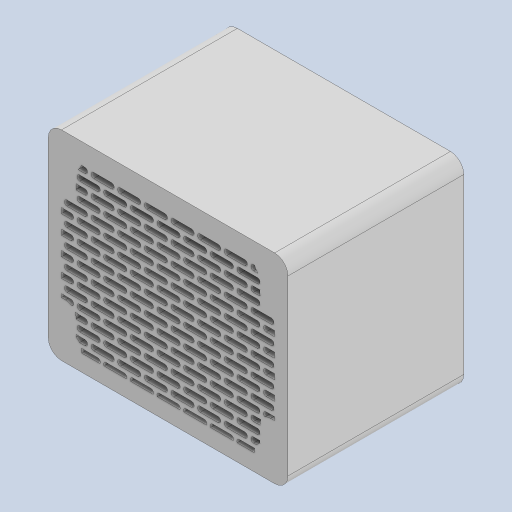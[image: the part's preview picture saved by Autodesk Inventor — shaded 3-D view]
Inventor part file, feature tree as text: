
AUTODESK INVENTOR PART (.ipt)
format: ipt  version: 2023 (Build 270158000, 158)  size: 2,324,480 bytes
history: native  units: mm
features: extrude x11, sketch x11, other x1
ambient origin geometry x8: Origin, YZ Plane, XZ Plane, XY Plane, X Axis, Y Axis, Z Axis, Center Point
bodies: Body1 (feature_tree)
feature tree (23):
  other  "Sólido1"
  extrude  "Extrusão1"  Depth=10.0mm
  extrude  "Extrusão2"  Depth=3.0mm
  extrude  "Extrusão3"  Depth=10.0mm
  extrude  "Extrusão4"  Depth=10.0mm
  extrude  "Extrusão5"  Depth=10.0mm
  extrude  "Extrusão6"  Depth=180.0mm
  extrude  "Extrusão7"  Depth=10.0mm
  extrude  "Extrusão8"  Depth=4.0mm TaperAngle=0.0deg
  extrude  "Extrusão9"  Depth=160.0mm
  sketch  "Esboço10"  dims[d49=10.0mm d50=2.5mm d51=3.0mm d52=2.5mm d53=4.0mm d54=128.0mm d55=0.0mm d56=0.0mm]
  extrude  "Extrusão10"  Depth=98.0mm
  extrude  "Extrusão11"  Depth=150.0mm
  sketch  "Esboço1"  dims[d4=10.0mm d8=2.5mm]
  sketch  "Esboço2"  dims[d12=3.0mm d13=2.5mm]
  sketch  "Esboço3"  dims[d14=4.0mm d15=0.0mm d16=10.0mm d17=2.5mm d18=3.0mm d19=2.5mm]
  sketch  "Esboço4"  dims[d20=10.0mm d21=0.0mm]
  sketch  "Esboço5"  dims[d22=10.0mm d23=2.5mm d24=3.0mm d25=2.5mm d26=5.0mm d27=0.0mm d28=10.0mm d29=2.5mm d30=3.0mm d31=2.5mm]
  sketch  "Esboço6"  dims[d32=70.0mm d33=0.0mm d34=10.0mm d35=2.5mm d36=3.0mm d37=2.5mm]
  sketch  "Esboço7"  dims[d38=7.0mm d39=0.0mm]
  sketch  "Esboço8"  dims[d40=10.0mm d41=2.5mm d42=3.0mm d43=2.5mm d44=45.0mm d45=0.0mm d46=180.0mm]
  sketch  "Esboço9"  dims[d47=150.0mm d48=10.0mm]
  sketch  "Esboço11"  dims[d64=128.0mm d65=0.0mm d66=6.0mm d67=45.0deg d68=2.0mm d71=6.0mm d72=0.0mm d73=160.0mm d74=98.0mm d75=150.0mm d76=125.0mm d77=6.0mm d78=45.0deg d79=2.0mm d80=160.0mm d81=98.0mm d82=150.0mm d83=125.0mm d86=10.0mm d87=70.0mm d89=20.0mm d90=30.0mm d92=20.0mm d95=100.0mm d97=14.0mm d98=10.0mm d100=10.0mm d102=10.0mm d103=2.5mm d104=3.0mm d105=2.5mm d106=10.0mm d107=2.5mm d108=3.0mm d109=2.5mm d110=160.0mm d111=125.0mm d112=10.0mm d113=4.0mm d114=0.0mm d115=4.0mm d116=0.0mm]
